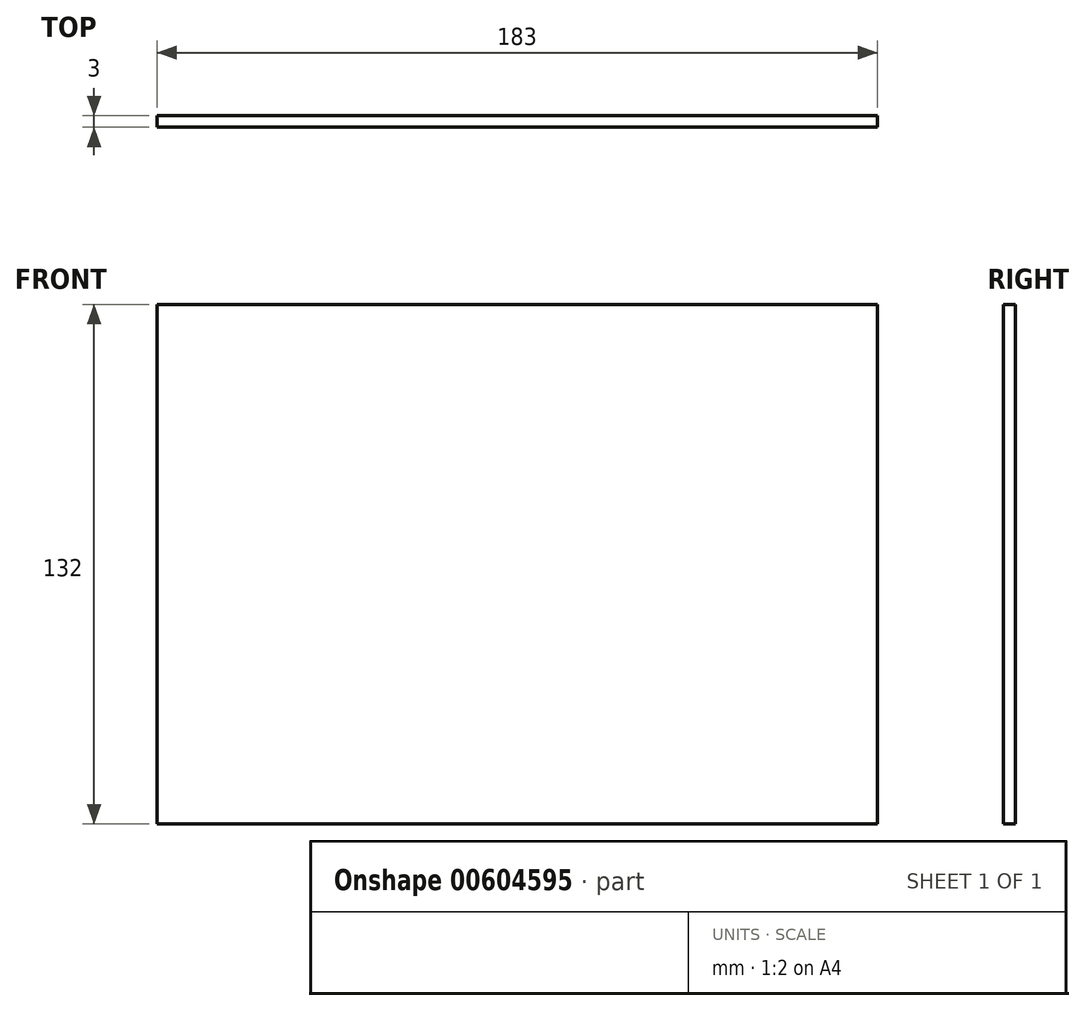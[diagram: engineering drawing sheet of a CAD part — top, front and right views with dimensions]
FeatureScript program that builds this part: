
annotation { "Feature Type Name" : "Feature", "Feature Type Description" : "" }
export const myFeature = defineFeature(function(context is Context, id is Id, definition is map)
    precondition{}
    {
        {
            var Q0;
            Q0=qCreatedBy(makeId("Front.planeOp"),FACE);
            var sketch = newSketch(context, id + "F0", { "sketchPlane" : qUnion([Q0])});
            skLineSegment(sketch, "E0", {"start": v(0, 0) * mm, "end": v(-74, 0) * mm});
            skLineSegment(sketch, "E1", {"start": v(-74, 0) * mm, "end": v(-74, 66) * mm});
            skLineSegment(sketch, "E2", {"start": v(-74, 66) * mm, "end": v(109, 66) * mm});
            skLineSegment(sketch, "E3", {"start": v(109, 66) * mm, "end": v(109, 0) * mm});
            skLineSegment(sketch, "E4", {"start": v(109, 0) * mm, "end": v(109, -66) * mm});
            skLineSegment(sketch, "E5", {"start": v(109, -66) * mm, "end": v(-74, -66) * mm});
            skLineSegment(sketch, "E6", {"start": v(-74, -66) * mm, "end": v(-74, 0) * mm});
            skSolve(sketch);
        }
        {
            var Q0;
            Q0 = qSketchRegion(id + "F0", true);
            extrude(context, id + "F1", {"entities" : qUnion([Q0]), "depth" : 3 * mm, "offsetDistance" : 25 * mm});
        }
    });
